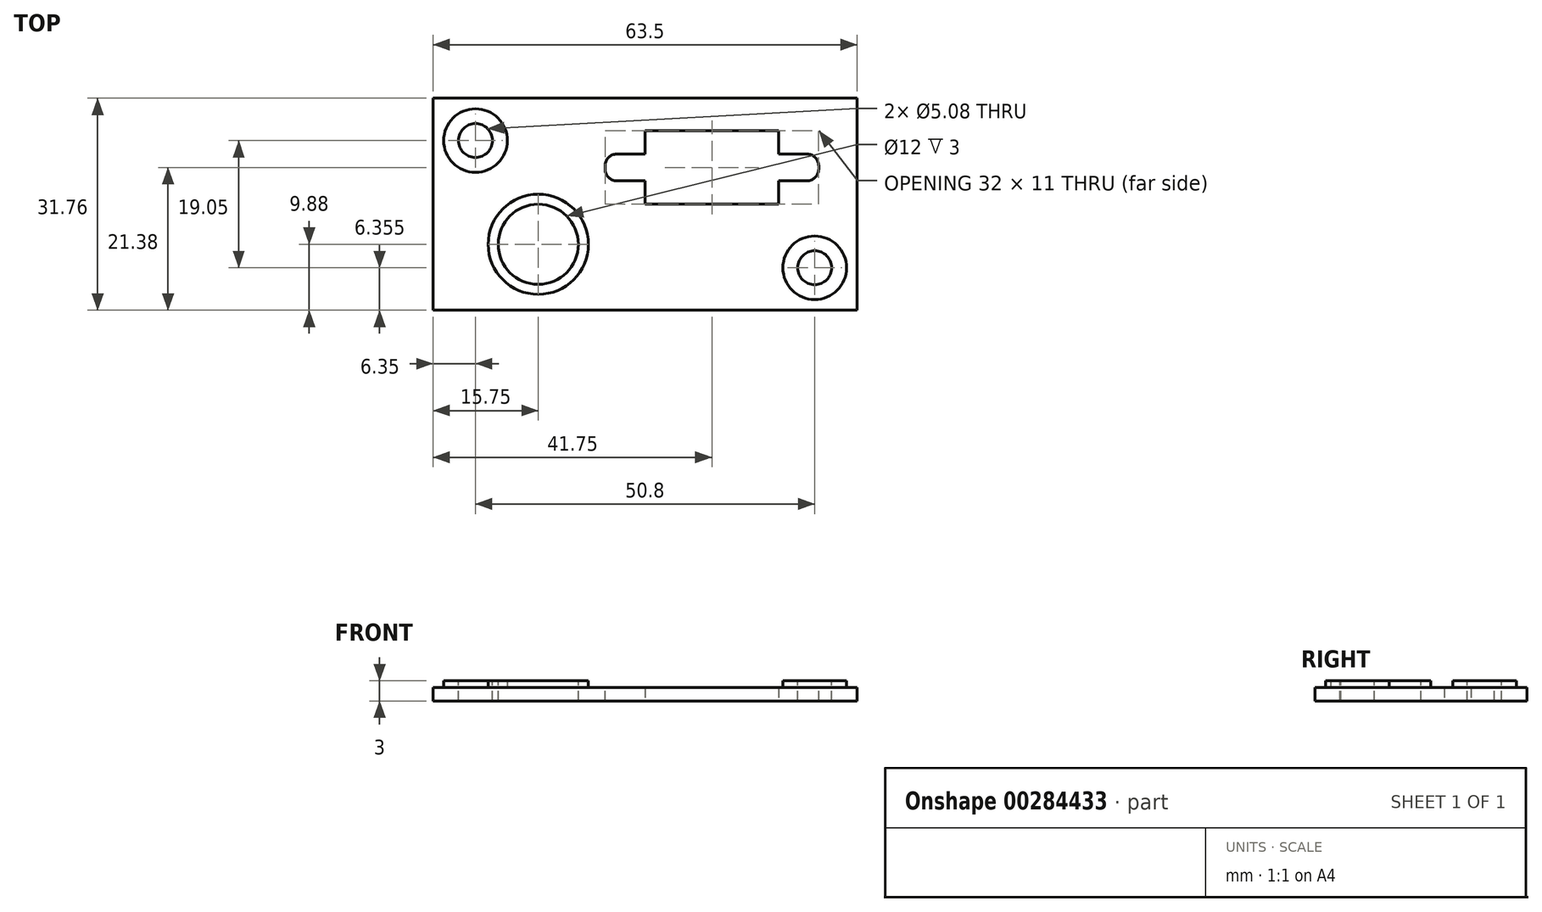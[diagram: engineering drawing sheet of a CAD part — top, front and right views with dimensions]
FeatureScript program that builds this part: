
annotation { "Feature Type Name" : "Feature", "Feature Type Description" : "" }
export const myFeature = defineFeature(function(context is Context, id is Id, definition is map)
    precondition{}
    {
        {
            var Q0;
            Q0=qCreatedBy(makeId("Top.planeOp"),FACE);
            var sketch = newSketch(context, id + "F0", { "sketchPlane" : qUnion([Q0])});
            skLineSegment(sketch, "E0.bottom", {"start": v(-31.75, 15.87) * mm, "end": v(31.75, 15.87) * mm});
            skLineSegment(sketch, "E0.top", {"start": v(-31.75, -15.87) * mm, "end": v(31.75, -15.87) * mm});
            skLineSegment(sketch, "E0.left", {"start": v(-31.75, 15.87) * mm, "end": v(-31.75, -15.87) * mm});
            skLineSegment(sketch, "E0.right", {"start": v(31.75, 15.87) * mm, "end": v(31.75, -15.87) * mm});
            skPoint(sketch, "E0.middle", {"position": v(0, 0) * mm});
            skSolve(sketch);
        }
        {
            var Q0;
            Q0 = qSketchRegion(id + "F0", true);
            extrude(context, id + "F1", {"entities" : qUnion([Q0]), "depth" : 2 * mm});
        }
        {
            var Q0;
            Q0=makeQuery(id+"F1.opExtrude","CAP_FACE",FACE,{"disambiguationData":[OSD([sQuery(id+"F0.wireOp",EDGE,"E0.bottom"),sQuery(id+"F0.wireOp",EDGE,"E0.top"),sQuery(id+"F0.wireOp",EDGE,"E0.left"),sQuery(id+"F0.wireOp",EDGE,"E0.right")])],"isStart":false});
            var sketch = newSketch(context, id + "F2", { "sketchPlane" : qUnion([Q0])});
            skLineSegment(sketch, "E1.bottom", {"start": v(-31.75, 15.87) * mm, "end": v(-25.4, 15.87) * mm});
            skLineSegment(sketch, "E1.top", {"start": v(-31.75, 9.52) * mm, "end": v(-25.4, 9.52) * mm});
            skLineSegment(sketch, "E1.left", {"start": v(-31.75, 15.87) * mm, "end": v(-31.75, 9.52) * mm});
            skLineSegment(sketch, "E1.right", {"start": v(-25.4, 15.87) * mm, "end": v(-25.4, 9.52) * mm});
            skLineSegment(sketch, "E2.bottom", {"start": v(31.75, -15.87) * mm, "end": v(25.4, -15.87) * mm});
            skLineSegment(sketch, "E2.top", {"start": v(31.75, -9.52) * mm, "end": v(25.4, -9.52) * mm});
            skLineSegment(sketch, "E2.left", {"start": v(31.75, -15.87) * mm, "end": v(31.75, -9.52) * mm});
            skLineSegment(sketch, "E2.right", {"start": v(25.4, -15.87) * mm, "end": v(25.4, -9.52) * mm});
            skSolve(sketch);
        }
        {
            var Q0;
            Q0=makeQuery(id+"F2.imprint","IMPRINT",FACE,{"disambiguationData":[TD([[makeQuery(id+"F2.imprint","IMPRINT",EDGE,{"derivedFrom":sQuery(id+"F2.wireOp",EDGE,"E1.bottom")}),-1.0]])]});
            var sketch = newSketch(context, id + "F3", { "sketchPlane" : qUnion([Q0])});
            skCircle(sketch, "E3", {"center": v(-25.4, 9.52) * mm, "radius": 4.76 * mm});
            skSolve(sketch);
        }
        {
            var Q0;
            Q0 = qSketchRegion(id + "F3", true);
            extrude(context, id + "F4", {"entities" : qUnion([Q0]), "operationType" : NewBodyOperationType.ADD, "depth" : 1 * mm});
        }
        {
            var Q0;
            Q0=makeQuery(id+"F2.imprint","IMPRINT",FACE,{"disambiguationData":[TD([[makeQuery(id+"F2.imprint","IMPRINT",EDGE,{"derivedFrom":sQuery(id+"F2.wireOp",EDGE,"E2.bottom")}),1.0]])]});
            var sketch = newSketch(context, id + "F5", { "sketchPlane" : qUnion([Q0])});
            skCircle(sketch, "E4", {"center": v(25.4, -9.52) * mm, "radius": 4.76 * mm});
            skSolve(sketch);
        }
        {
            var Q0;
            Q0=makeQuery(id+"F4.opExtrude","CAP_FACE",FACE,{"disambiguationData":[OSD([sQuery(id+"F3.wireOp",EDGE,"E3")])],"isStart":false});
            var sketch = newSketch(context, id + "F6", { "sketchPlane" : qUnion([Q0])});
            skCircle(sketch, "E5", {"center": v(-25.4, 9.52) * mm, "radius": 2.54 * mm});
            skSolve(sketch);
        }
        {
            var Q0;
            Q0 = qSketchRegion(id + "F6", true);
            extrude(context, id + "F7", {"entities" : qUnion([Q0]), "operationType" : NewBodyOperationType.REMOVE, "oppositeDirection" : true, "depth" : 25.4 * mm});
        }
        {
            var Q0;
            {var subQ3=sQuery(id+"F2.wireOp",EDGE,"E1.top");Q0=makeQuery(id+"F2.imprint","IMPRINT",FACE,{"disambiguationData":[TD([[makeQuery(id+"F2.imprint","IMPRINT",EDGE,{"derivedFrom":subQ3}),-1.0]])]});}
            var sketch = newSketch(context, id + "F8", { "sketchPlane" : qUnion([Q0])});
            skLineSegment(sketch, "E6.bottom", {"start": v(0, 11) * mm, "end": v(20, 11) * mm});
            skLineSegment(sketch, "E6.top", {"start": v(0, 0) * mm, "end": v(20, 0) * mm});
            skLineSegment(sketch, "E6.left", {"start": v(0, 11) * mm, "end": v(0, 0) * mm});
            skLineSegment(sketch, "E6.right", {"start": v(20, 11) * mm, "end": v(20, 0) * mm});
            skSolve(sketch);
        }
        {
            var Q0;
            Q0 = qSketchRegion(id + "F8", true);
            extrude(context, id + "F9", {"entities" : qUnion([Q0]), "operationType" : NewBodyOperationType.REMOVE, "oppositeDirection" : true, "depth" : 25 * mm});
        }
        {
            var Q0;
            {var subQ3=sQuery(id+"F2.wireOp",EDGE,"E1.top");Q0=makeQuery(id+"F2.imprint","IMPRINT",FACE,{"disambiguationData":[TD([[makeQuery(id+"F2.imprint","IMPRINT",EDGE,{"derivedFrom":subQ3}),-1.0]])]});}
            var sketch = newSketch(context, id + "F10", { "sketchPlane" : qUnion([Q0])});
            skLineSegment(sketch, "E7.bottom", {"start": v(0, 0) * mm, "end": v(-16, 0) * mm, "construction": true});
            skLineSegment(sketch, "E7.top", {"start": v(0, -6) * mm, "end": v(-16, -6) * mm, "construction": true});
            skLineSegment(sketch, "E7.left", {"start": v(0, 0) * mm, "end": v(0, -6) * mm, "construction": true});
            skLineSegment(sketch, "E7.right", {"start": v(-16, 0) * mm, "end": v(-16, -6) * mm, "construction": true});
            skSolve(sketch);
        }
        {
            var Q0;
            {var subQ3=sQuery(id+"F2.wireOp",EDGE,"E1.top");Q0=makeQuery(id+"F2.imprint","IMPRINT",FACE,{"disambiguationData":[TD([[makeQuery(id+"F2.imprint","IMPRINT",EDGE,{"derivedFrom":subQ3}),-1.0]])]});}
            var sketch = newSketch(context, id + "F11", { "sketchPlane" : qUnion([Q0])});
            skCircle(sketch, "E8", {"center": v(-16, -6) * mm, "radius": 7.5 * mm});
            skSolve(sketch);
        }
        {
            var Q0;
            Q0 = qSketchRegion(id + "F11", true);
            extrude(context, id + "F12", {"entities" : qUnion([Q0]), "operationType" : NewBodyOperationType.ADD, "depth" : 1 * mm});
        }
        {
            var Q0;
            Q0=makeQuery(id+"F12.opExtrude","CAP_FACE",FACE,{"disambiguationData":[OSD([sQuery(id+"F11.wireOp",EDGE,"E8")])],"isStart":false});
            var sketch = newSketch(context, id + "F13", { "sketchPlane" : qUnion([Q0])});
            skCircle(sketch, "E9", {"center": v(-16, -6) * mm, "radius": 6 * mm});
            skSolve(sketch);
        }
        {
            var Q0;
            Q0 = qSketchRegion(id + "F13", true);
            extrude(context, id + "F14", {"entities" : qUnion([Q0]), "operationType" : NewBodyOperationType.REMOVE, "oppositeDirection" : true, "depth" : 25 * mm});
        }
        {
            var Q0;
            Q0 = qSketchRegion(id + "F5", true);
            extrude(context, id + "F15", {"entities" : qUnion([Q0]), "operationType" : NewBodyOperationType.ADD, "depth" : 1 * mm});
        }
        {
            var Q0;
            Q0=makeQuery(id+"F15.opExtrude","CAP_FACE",FACE,{"disambiguationData":[OSD([sQuery(id+"F5.wireOp",EDGE,"E4")])],"isStart":false});
            var sketch = newSketch(context, id + "F16", { "sketchPlane" : qUnion([Q0])});
            skCircle(sketch, "E10", {"center": v(25.4, -9.52) * mm, "radius": 2.54 * mm});
            skSolve(sketch);
        }
        {
            var Q0;
            Q0 = qSketchRegion(id + "F16", true);
            extrude(context, id + "F17", {"entities" : qUnion([Q0]), "operationType" : NewBodyOperationType.REMOVE, "oppositeDirection" : true, "depth" : 25.4 * mm});
        }
        {
            var Q0;
            {var subQ3=sQuery(id+"F2.wireOp",EDGE,"E1.top");Q0=makeQuery(id+"F10.imprint","IMPRINT",FACE,{"disambiguationData":[TD([[makeQuery(id+"F10.imprint","IMPRINT",EDGE,{"derivedFrom":makeQuery(id+"F2.imprint","IMPRINT",EDGE,{"derivedFrom":subQ3})}),-1.0]])]});}
            var sketch = newSketch(context, id + "F18", { "sketchPlane" : qUnion([Q0])});
            skLineSegment(sketch, "E11.bottom", {"start": v(6, 7.5) * mm, "end": v(-4.25, 7.5) * mm});
            skLineSegment(sketch, "E11.top", {"start": v(6, 3.5) * mm, "end": v(-4.25, 3.5) * mm});
            skLineSegment(sketch, "E11.left", {"start": v(6, 7.5) * mm, "end": v(6, 3.5) * mm});
            skLineSegment(sketch, "E11.right", {"start": v(-6, 5.75) * mm, "end": v(-6, 5.25) * mm});
            skPoint(sketch, "E11.middle", {"position": v(0, 5.5) * mm});
            skPoint(sketch, "E12.visualSharp", {"position": v(-6, 7.5) * mm});
            skArc(sketch, "E12.filletArc", {"start": v(-4.25, 7.5) * mm, "mid": v(-5.49, 6.99) * mm, "end": v(-6, 5.75) * mm});
            skLineSegment(sketch, "E13.bottom", {"start": v(24.25, 3.5) * mm, "end": v(14, 3.5) * mm});
            skLineSegment(sketch, "E13.top", {"start": v(24.25, 7.5) * mm, "end": v(14, 7.5) * mm});
            skLineSegment(sketch, "E13.left", {"start": v(26, 5.25) * mm, "end": v(26, 5.75) * mm});
            skLineSegment(sketch, "E13.right", {"start": v(14, 3.5) * mm, "end": v(14, 7.5) * mm});
            skPoint(sketch, "E13.middle", {"position": v(20, 5.5) * mm});
            skPoint(sketch, "E14.visualSharp", {"position": v(26, 7.5) * mm});
            skArc(sketch, "E14.filletArc", {"start": v(26, 5.75) * mm, "mid": v(25.49, 6.99) * mm, "end": v(24.25, 7.5) * mm});
            skPoint(sketch, "E15.visualSharp", {"position": v(26, 3.5) * mm});
            skArc(sketch, "E15.filletArc", {"start": v(24.25, 3.5) * mm, "mid": v(25.49, 4.01) * mm, "end": v(26, 5.25) * mm});
            skPoint(sketch, "E16.visualSharp", {"position": v(-6, 3.5) * mm});
            skArc(sketch, "E16.filletArc", {"start": v(-6, 5.25) * mm, "mid": v(-5.49, 4.01) * mm, "end": v(-4.25, 3.5) * mm});
            skSolve(sketch);
        }
        {
            var Q0;
            Q0 = qSketchRegion(id + "F18", true);
            extrude(context, id + "F19", {"entities" : qUnion([Q0]), "operationType" : NewBodyOperationType.REMOVE, "oppositeDirection" : true, "depth" : 25 * mm});
        }
    });
